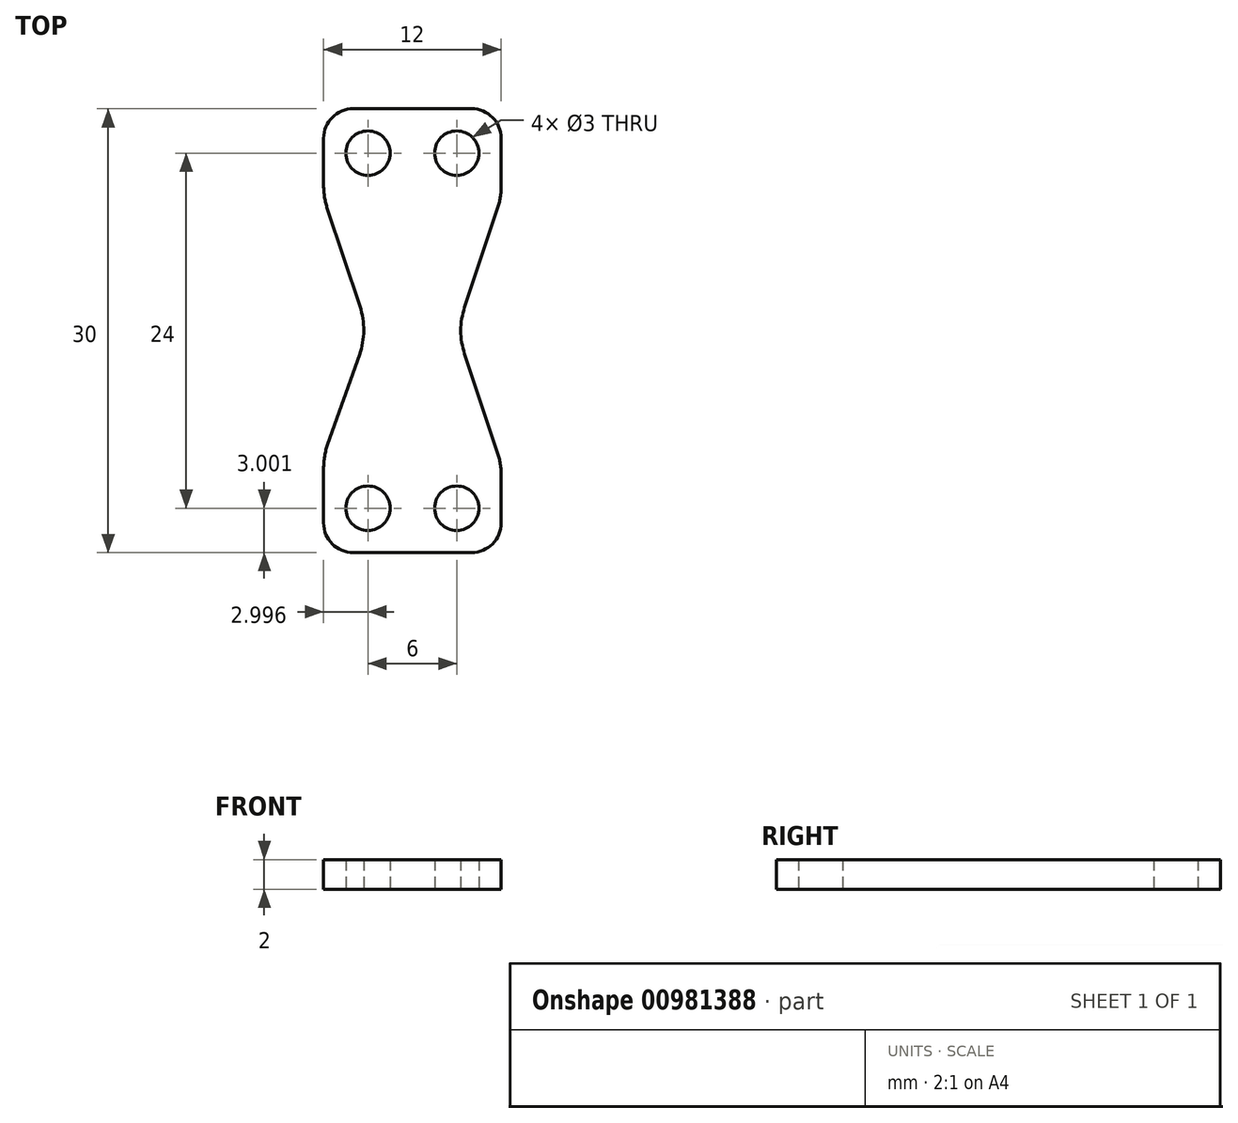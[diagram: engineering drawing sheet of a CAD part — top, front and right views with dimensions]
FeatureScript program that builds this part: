
annotation { "Feature Type Name" : "Feature", "Feature Type Description" : "" }
export const myFeature = defineFeature(function(context is Context, id is Id, definition is map)
    precondition{}
    {
        {
            var Q0;
            Q0=qCreatedBy(makeId("Top.planeOp"),FACE);
            var sketch = newSketch(context, id + "F0", { "sketchPlane" : qUnion([Q0])});
            skCircle(sketch, "E0", {"center": v(-54.21, -20.46) * mm, "radius": 1.5 * mm});
            skCircle(sketch, "E1.0.1.0", {"center": v(-54.21, 3.54) * mm, "radius": 1.5 * mm});
            skCircle(sketch, "E1.1.0.0", {"center": v(-48.21, -20.46) * mm, "radius": 1.5 * mm});
            skCircle(sketch, "E1.1.1.0", {"center": v(-48.21, 3.54) * mm, "radius": 1.5 * mm});
            skLineSegment(sketch, "E1.direction1", {"start": v(-54.21, -20.46) * mm, "end": v(-48.21, -20.46) * mm, "construction": true});
            skLineSegment(sketch, "E1.direction2", {"start": v(-54.21, -20.46) * mm, "end": v(-54.21, 3.54) * mm, "construction": true});
            skLineSegment(sketch, "E2", {"start": v(-55.21, -23.46) * mm, "end": v(-47.21, -23.46) * mm});
            skLineSegment(sketch, "E3", {"start": v(-45.21, -21.46) * mm, "end": v(-45.21, -18.27) * mm});
            skLineSegment(sketch, "E4", {"start": v(-45.47, -16.69) * mm, "end": v(-47.69, -10.04) * mm});
            skLineSegment(sketch, "E5", {"start": v(-47.69, -6.88) * mm, "end": v(-45.47, -0.23) * mm});
            skLineSegment(sketch, "E6", {"start": v(-45.21, 1.35) * mm, "end": v(-45.21, 4.54) * mm});
            skLineSegment(sketch, "E7", {"start": v(-47.21, 6.54) * mm, "end": v(-55.21, 6.54) * mm});
            skLineSegment(sketch, "E8", {"start": v(-57.21, -21.46) * mm, "end": v(-57.21, -17.78) * mm});
            skLineSegment(sketch, "E9", {"start": v(-56.93, -16.11) * mm, "end": v(-54.79, -10.08) * mm});
            skLineSegment(sketch, "E10", {"start": v(-54.76, -6.83) * mm, "end": v(-56.96, -0.23) * mm});
            skLineSegment(sketch, "E11", {"start": v(-57.21, 1.35) * mm, "end": v(-57.21, 4.54) * mm});
            skPoint(sketch, "E12.visualSharp", {"position": v(-57.21, 6.54) * mm});
            skArc(sketch, "E12.filletArc", {"start": v(-55.21, 6.54) * mm, "mid": v(-56.63, 5.95) * mm, "end": v(-57.21, 4.54) * mm});
            skPoint(sketch, "E13.visualSharp", {"position": v(-45.21, 6.54) * mm});
            skArc(sketch, "E13.filletArc", {"start": v(-45.21, 4.54) * mm, "mid": v(-45.8, 5.95) * mm, "end": v(-47.21, 6.54) * mm});
            skPoint(sketch, "E14.visualSharp", {"position": v(-45.21, -23.46) * mm});
            skArc(sketch, "E14.filletArc", {"start": v(-47.21, -23.46) * mm, "mid": v(-45.8, -22.87) * mm, "end": v(-45.21, -21.46) * mm});
            skPoint(sketch, "E15.visualSharp", {"position": v(-57.21, -23.46) * mm});
            skArc(sketch, "E15.filletArc", {"start": v(-57.21, -21.46) * mm, "mid": v(-56.63, -22.87) * mm, "end": v(-55.21, -23.46) * mm});
            skPoint(sketch, "E16.visualSharp", {"position": v(-57.21, -16.92) * mm});
            skArc(sketch, "E16.filletArc", {"start": v(-56.93, -16.11) * mm, "mid": v(-57.14, -16.94) * mm, "end": v(-57.21, -17.78) * mm});
            skPoint(sketch, "E17.visualSharp", {"position": v(-45.21, -17.46) * mm});
            skArc(sketch, "E17.filletArc", {"start": v(-45.21, -18.27) * mm, "mid": v(-45.28, -17.47) * mm, "end": v(-45.47, -16.69) * mm});
            skPoint(sketch, "E18.visualSharp", {"position": v(-45.21, 0.54) * mm});
            skArc(sketch, "E18.filletArc", {"start": v(-45.47, -0.23) * mm, "mid": v(-45.28, 0.55) * mm, "end": v(-45.21, 1.35) * mm});
            skPoint(sketch, "E19.visualSharp", {"position": v(-57.21, 0.54) * mm});
            skArc(sketch, "E19.filletArc", {"start": v(-57.21, 1.35) * mm, "mid": v(-57.15, 0.55) * mm, "end": v(-56.96, -0.23) * mm});
            skPoint(sketch, "E20.visualSharp", {"position": v(-48.21, -8.46) * mm});
            skArc(sketch, "E20.filletArc", {"start": v(-47.69, -6.88) * mm, "mid": v(-47.94, -8.46) * mm, "end": v(-47.69, -10.04) * mm});
            skPoint(sketch, "E21.visualSharp", {"position": v(-54.21, -8.46) * mm});
            skArc(sketch, "E21.filletArc", {"start": v(-54.79, -10.08) * mm, "mid": v(-54.5, -8.46) * mm, "end": v(-54.76, -6.83) * mm});
            skSolve(sketch);
        }
        {
            var Q0;
            Q0=makeQuery(id+"F0.imprint","IMPRINT",FACE,{"disambiguationData":[TD([[makeQuery(id+"F0.imprint","IMPRINT",EDGE,{"derivedFrom":sQuery(id+"F0.wireOp",EDGE,"E0")}),-1.0]])]});
            extrude(context, id + "F1", {"entities" : qUnion([Q0]), "depth" : 2 * mm, "offsetDistance" : 25 * mm});
        }
    });
